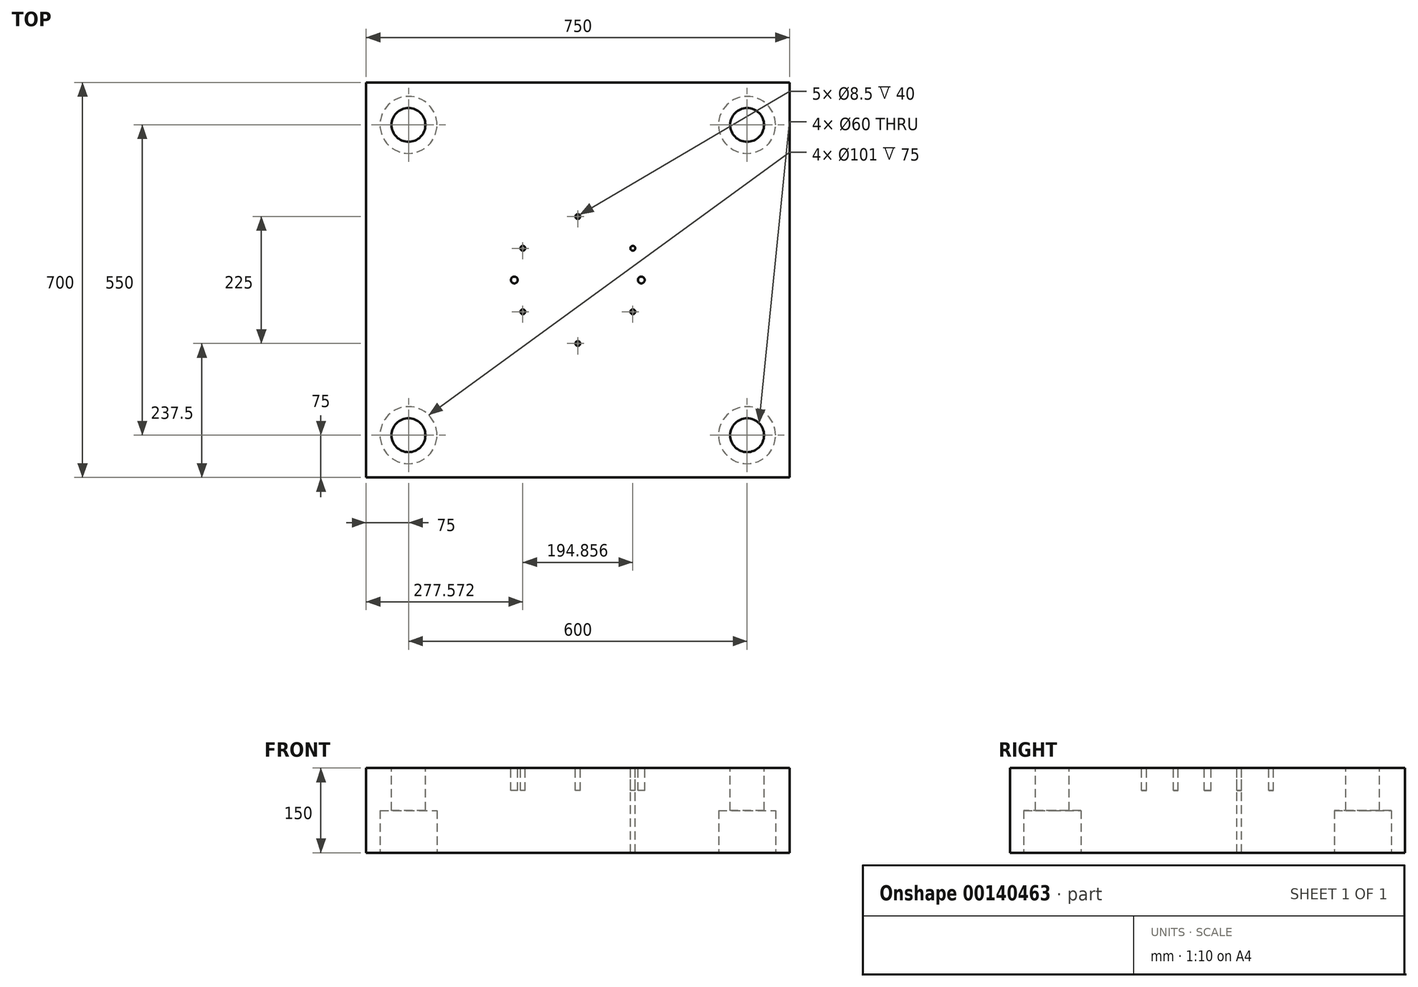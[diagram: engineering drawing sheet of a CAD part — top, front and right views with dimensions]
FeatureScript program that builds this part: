
annotation { "Feature Type Name" : "Feature", "Feature Type Description" : "" }
export const myFeature = defineFeature(function(context is Context, id is Id, definition is map)
    precondition{}
    {
        {
            var Q0;
            Q0=qCreatedBy(makeId("Top.planeOp"),FACE);
            var sketch = newSketch(context, id + "F0", { "sketchPlane" : qUnion([Q0])});
            skLineSegment(sketch, "E0.bottom", {"start": v(375, -350) * mm, "end": v(-375, -350) * mm});
            skLineSegment(sketch, "E0.top", {"start": v(375, 350) * mm, "end": v(-375, 350) * mm});
            skLineSegment(sketch, "E0.left", {"start": v(375, -350) * mm, "end": v(375, 350) * mm});
            skLineSegment(sketch, "E0.right", {"start": v(-375, -350) * mm, "end": v(-375, 350) * mm});
            skPoint(sketch, "E0.middle", {"position": v(0, 0) * mm});
            skCircle(sketch, "E1", {"center": v(-300, -275) * mm, "radius": 30 * mm});
            skCircle(sketch, "E2", {"center": v(300, -275) * mm, "radius": 30 * mm});
            skCircle(sketch, "E3", {"center": v(300, 275) * mm, "radius": 30 * mm});
            skCircle(sketch, "E4", {"center": v(-300, 275) * mm, "radius": 30 * mm});
            skCircle(sketch, "E5", {"center": v(0, 0) * mm, "radius": 112.5 * mm, "construction": true});
            skCircle(sketch, "E6", {"center": v(0, 112.5) * mm, "radius": 4.25 * mm});
            skCircle(sketch, "E7.1.0", {"center": v(-97.43, 56.25) * mm, "radius": 4.25 * mm});
            skCircle(sketch, "E7.2.0", {"center": v(-97.43, -56.25) * mm, "radius": 4.25 * mm});
            skCircle(sketch, "E7.3.0", {"center": v(0, -112.5) * mm, "radius": 4.25 * mm});
            skCircle(sketch, "E7.4.0", {"center": v(97.43, -56.25) * mm, "radius": 4.25 * mm});
            skCircle(sketch, "E7.5.0", {"center": v(97.43, 56.25) * mm, "radius": 4.25 * mm});
            skCircle(sketch, "E8", {"center": v(-112.5, 0) * mm, "radius": 6 * mm});
            skCircle(sketch, "E9", {"center": v(112.5, 0) * mm, "radius": 6 * mm});
            skSolve(sketch);
        }
        {
            var Q0;
            Q0=makeQuery(id+"F0.imprint","IMPRINT",FACE,{"disambiguationData":[TD([[makeQuery(id+"F0.imprint","IMPRINT",EDGE,{"derivedFrom":sQuery(id+"F0.wireOp",EDGE,"E0.bottom")}),-1.0]])]});
            var Q1;
            Q1=makeQuery(id+"F0.imprint","IMPRINT",FACE,{"disambiguationData":[TD([[makeQuery(id+"F0.imprint","IMPRINT",EDGE,{"derivedFrom":sQuery(id+"F0.wireOp",EDGE,"E8")}),1.0]])]});
            var Q2;
            Q2=makeQuery(id+"F0.imprint","IMPRINT",FACE,{"disambiguationData":[TD([[makeQuery(id+"F0.imprint","IMPRINT",EDGE,{"derivedFrom":sQuery(id+"F0.wireOp",EDGE,"E7.2.0")}),1.0]])]});
            var Q3;
            Q3=makeQuery(id+"F0.imprint","IMPRINT",FACE,{"disambiguationData":[TD([[makeQuery(id+"F0.imprint","IMPRINT",EDGE,{"derivedFrom":sQuery(id+"F0.wireOp",EDGE,"E7.1.0")}),1.0]])]});
            var Q4;
            Q4=makeQuery(id+"F0.imprint","IMPRINT",FACE,{"disambiguationData":[TD([[makeQuery(id+"F0.imprint","IMPRINT",EDGE,{"derivedFrom":sQuery(id+"F0.wireOp",EDGE,"E6")}),1.0]])]});
            var Q5;
            Q5=makeQuery(id+"F0.imprint","IMPRINT",FACE,{"disambiguationData":[TD([[makeQuery(id+"F0.imprint","IMPRINT",EDGE,{"derivedFrom":sQuery(id+"F0.wireOp",EDGE,"E9")}),1.0]])]});
            var Q6;
            Q6=makeQuery(id+"F0.imprint","IMPRINT",FACE,{"disambiguationData":[TD([[makeQuery(id+"F0.imprint","IMPRINT",EDGE,{"derivedFrom":sQuery(id+"F0.wireOp",EDGE,"E7.4.0")}),1.0]])]});
            var Q7;
            Q7=makeQuery(id+"F0.imprint","IMPRINT",FACE,{"disambiguationData":[TD([[makeQuery(id+"F0.imprint","IMPRINT",EDGE,{"derivedFrom":sQuery(id+"F0.wireOp",EDGE,"E7.3.0")}),1.0]])]});
            extrude(context, id + "F1", {"entities" : qUnion([Q0, Q1, Q2, Q3, Q4, Q5, Q6, Q7]), "oppositeDirection" : true, "depth" : 150 * mm});
        }
        {
            var Q0;
            Q0=makeQuery(id+"F0.imprint","IMPRINT",FACE,{"disambiguationData":[TD([[makeQuery(id+"F0.imprint","IMPRINT",EDGE,{"derivedFrom":sQuery(id+"F0.wireOp",EDGE,"E4")}),-1.0]])]});
            var Q1;
            Q1=makeQuery(id+"F0.imprint","IMPRINT",FACE,{"disambiguationData":[TD([[makeQuery(id+"F0.imprint","IMPRINT",EDGE,{"derivedFrom":sQuery(id+"F0.wireOp",EDGE,"E3")}),-1.0]])]});
            var Q2;
            Q2=makeQuery(id+"F0.imprint","IMPRINT",FACE,{"disambiguationData":[TD([[makeQuery(id+"F0.imprint","IMPRINT",EDGE,{"derivedFrom":sQuery(id+"F0.wireOp",EDGE,"E2")}),-1.0]])]});
            var Q3;
            Q3=makeQuery(id+"F0.imprint","IMPRINT",FACE,{"disambiguationData":[TD([[makeQuery(id+"F0.imprint","IMPRINT",EDGE,{"derivedFrom":sQuery(id+"F0.wireOp",EDGE,"E1")}),-1.0]])]});
            extrude(context, id + "F2", {"entities" : qUnion([Q0, Q1, Q2, Q3]), "oppositeDirection" : true, "depth" : 130 * mm});
        }
        {
            var Q0;
            Q0=makeQuery(id+"F0.imprint","IMPRINT",FACE,{"disambiguationData":[TD([[makeQuery(id+"F0.imprint","IMPRINT",EDGE,{"derivedFrom":sQuery(id+"F0.wireOp",EDGE,"E8")}),1.0]])]});
            var Q1;
            Q1=makeQuery(id+"F0.imprint","IMPRINT",FACE,{"disambiguationData":[TD([[makeQuery(id+"F0.imprint","IMPRINT",EDGE,{"derivedFrom":sQuery(id+"F0.wireOp",EDGE,"E7.1.0")}),1.0]])]});
            var Q2;
            Q2=makeQuery(id+"F0.imprint","IMPRINT",FACE,{"disambiguationData":[TD([[makeQuery(id+"F0.imprint","IMPRINT",EDGE,{"derivedFrom":sQuery(id+"F0.wireOp",EDGE,"E6")}),1.0]])]});
            var Q3;
            Q3=makeQuery(id+"F0.imprint","IMPRINT",FACE,{"disambiguationData":[TD([[makeQuery(id+"F0.imprint","IMPRINT",EDGE,{"derivedFrom":sQuery(id+"F0.wireOp",EDGE,"E7.5.0")}),1.0]])]});
            var Q4;
            Q4=makeQuery(id+"F0.imprint","IMPRINT",FACE,{"disambiguationData":[TD([[makeQuery(id+"F0.imprint","IMPRINT",EDGE,{"derivedFrom":sQuery(id+"F0.wireOp",EDGE,"E9")}),1.0]])]});
            var Q5;
            Q5=makeQuery(id+"F0.imprint","IMPRINT",FACE,{"disambiguationData":[TD([[makeQuery(id+"F0.imprint","IMPRINT",EDGE,{"derivedFrom":sQuery(id+"F0.wireOp",EDGE,"E7.4.0")}),1.0]])]});
            var Q6;
            Q6=makeQuery(id+"F0.imprint","IMPRINT",FACE,{"disambiguationData":[TD([[makeQuery(id+"F0.imprint","IMPRINT",EDGE,{"derivedFrom":sQuery(id+"F0.wireOp",EDGE,"E7.3.0")}),1.0]])]});
            var Q7;
            Q7=makeQuery(id+"F0.imprint","IMPRINT",FACE,{"disambiguationData":[TD([[makeQuery(id+"F0.imprint","IMPRINT",EDGE,{"derivedFrom":sQuery(id+"F0.wireOp",EDGE,"E7.2.0")}),1.0]])]});
            extrude(context, id + "F3", {"entities" : qUnion([Q0, Q1, Q2, Q3, Q4, Q5, Q6, Q7]), "operationType" : NewBodyOperationType.REMOVE, "oppositeDirection" : true, "depth" : 40 * mm});
        }
        {
            var Q0;
            Q0=makeQuery(id+"F2.opExtrude","SWEPT_BODY",BODY,{"disambiguationData":[OSD([sQuery(id+"F0.wireOp",EDGE,"E3"),sQuery(id+"F0.wireOp",EDGE,"0WcaU4d4-yjLl-t4DH-PHqA-r2zW4oB6RqLG")])]});
            var Q1;
            Q1=makeQuery(id+"F2.opExtrude","SWEPT_BODY",BODY,{"disambiguationData":[OSD([sQuery(id+"F0.wireOp",EDGE,"E2"),sQuery(id+"F0.wireOp",EDGE,"WCeEpNrA-Mq1f-Tu2g-0Etf-8BQyyMGswOfX")])]});
            var Q2;
            Q2=makeQuery(id+"F2.opExtrude","SWEPT_BODY",BODY,{"disambiguationData":[OSD([sQuery(id+"F0.wireOp",EDGE,"E1"),sQuery(id+"F0.wireOp",EDGE,"xFfE00Wn-gLOv-J7tR-mGqZ-GsZgmZ165pkX")])]});
            var Q3;
            Q3=makeQuery(id+"F2.opExtrude","SWEPT_BODY",BODY,{"disambiguationData":[OSD([sQuery(id+"F0.wireOp",EDGE,"E4"),sQuery(id+"F0.wireOp",EDGE,"XaCNIt4j-slsJ-z5ex-szqA-43I0Ko6RFmIr")])]});
            transform(context, id + "F4", {"entities" : qUnion([Q0, Q1, Q2, Q3]), "transformType" : TransformType.TRANSLATION_3D, "dx" : 0 * mm, "dy" : 0 * mm, "dz" : -20 * mm, "makeCopy" : false});
        }
        {
            var Q0;
            Q0=makeQuery(id+"F2.opExtrude","SWEPT_BODY",BODY,{"disambiguationData":[OSD([sQuery(id+"F0.wireOp",EDGE,"E3"),sQuery(id+"F0.wireOp",EDGE,"0WcaU4d4-yjLl-t4DH-PHqA-r2zW4oB6RqLG")])]});
            var Q1;
            Q1=makeQuery(id+"F2.opExtrude","SWEPT_BODY",BODY,{"disambiguationData":[OSD([sQuery(id+"F0.wireOp",EDGE,"E2"),sQuery(id+"F0.wireOp",EDGE,"WCeEpNrA-Mq1f-Tu2g-0Etf-8BQyyMGswOfX")])]});
            var Q2;
            Q2=makeQuery(id+"F2.opExtrude","SWEPT_BODY",BODY,{"disambiguationData":[OSD([sQuery(id+"F0.wireOp",EDGE,"E4"),sQuery(id+"F0.wireOp",EDGE,"XaCNIt4j-slsJ-z5ex-szqA-43I0Ko6RFmIr")])]});
            var Q3;
            Q3=makeQuery(id+"F2.opExtrude","SWEPT_BODY",BODY,{"disambiguationData":[OSD([sQuery(id+"F0.wireOp",EDGE,"E1"),sQuery(id+"F0.wireOp",EDGE,"xFfE00Wn-gLOv-J7tR-mGqZ-GsZgmZ165pkX")])]});
            var Q4;
            Q4=makeQuery(id+"F1.opExtrude","SWEPT_BODY",BODY,{"disambiguationData":[OSD([sQuery(id+"F0.wireOp",EDGE,"E0.bottom"),sQuery(id+"F0.wireOp",EDGE,"E0.top"),sQuery(id+"F0.wireOp",EDGE,"E0.left"),sQuery(id+"F0.wireOp",EDGE,"E0.right"),sQuery(id+"F0.wireOp",EDGE,"xFfE00Wn-gLOv-J7tR-mGqZ-GsZgmZ165pkX"),sQuery(id+"F0.wireOp",EDGE,"XaCNIt4j-slsJ-z5ex-szqA-43I0Ko6RFmIr"),sQuery(id+"F0.wireOp",EDGE,"WCeEpNrA-Mq1f-Tu2g-0Etf-8BQyyMGswOfX"),sQuery(id+"F0.wireOp",EDGE,"0WcaU4d4-yjLl-t4DH-PHqA-r2zW4oB6RqLG"),sQuery(id+"F0.wireOp",EDGE,"E7.5.0")])]});
            booleanBodies(context, id + "F5", {"operationType" : BooleanOperationType.UNION, "tools" : qUnion([Q0, Q1, Q2, Q3, Q4])});
        }
        {
            var Q0;
            {var subQ0=sQuery(id+"F0.wireOp",EDGE,"E7.5.0");var subQ1=sQuery(id+"F0.wireOp",EDGE,"E4");var subQ2=sQuery(id+"F0.wireOp",EDGE,"E3");var subQ3=sQuery(id+"F0.wireOp",EDGE,"E2");var subQ4=sQuery(id+"F0.wireOp",EDGE,"E1");var subQ5=sQuery(id+"F0.wireOp",EDGE,"E0.right");var subQ6=sQuery(id+"F0.wireOp",EDGE,"E0.left");var subQ7=sQuery(id+"F0.wireOp",EDGE,"E0.top");var subQ8=sQuery(id+"F0.wireOp",EDGE,"E0.bottom");Q0=makeQuery(id+"F5.opBoolean","MERGE",FACE,{"derivedFrom":[makeQuery(id+"F1.opExtrude","CAP_FACE",FACE,{"disambiguationData":[OSD([subQ8,subQ7,subQ6,subQ5,subQ4,subQ3,subQ2,subQ1,subQ0])],"isStart":false}),makeQuery(id+"F2.opExtrude","CAP_FACE",FACE,{"disambiguationData":[OSD([subQ8,subQ7,subQ6,subQ5,subQ4,subQ3,subQ2,subQ1,sQuery(id+"F0.wireOp",EDGE,"E6"),sQuery(id+"F0.wireOp",EDGE,"E7.1.0"),sQuery(id+"F0.wireOp",EDGE,"E7.2.0"),sQuery(id+"F0.wireOp",EDGE,"E7.3.0"),sQuery(id+"F0.wireOp",EDGE,"E7.4.0"),subQ0,sQuery(id+"F0.wireOp",EDGE,"E8"),sQuery(id+"F0.wireOp",EDGE,"E9")])],"isStart":false})]});}
            var sketch = newSketch(context, id + "F6", { "sketchPlane" : qUnion([Q0])});
            skPoint(sketch, "E10", {"position": v(-300, 275) * mm});
            skPoint(sketch, "E11", {"position": v(300, 275) * mm});
            skPoint(sketch, "E12", {"position": v(300, -275) * mm});
            skPoint(sketch, "E13", {"position": v(-300, -275) * mm});
            skCircle(sketch, "E14", {"center": v(-300, 275) * mm, "radius": 50.5 * mm});
            skCircle(sketch, "E15", {"center": v(-300, -275) * mm, "radius": 50.5 * mm});
            skCircle(sketch, "E16", {"center": v(300, -275) * mm, "radius": 50.5 * mm});
            skCircle(sketch, "E17", {"center": v(300, 275) * mm, "radius": 50.5 * mm});
            skSolve(sketch);
        }
        {
            var Q0;
            Q0=makeQuery(id+"F6.imprint","IMPRINT",FACE,{"disambiguationData":[TD([[makeQuery(id+"F6.imprint","IMPRINT",EDGE,{"derivedFrom":sQuery(id+"F6.wireOp",EDGE,"E14")}),1.0]])]});
            var Q1;
            Q1=makeQuery(id+"F6.imprint","IMPRINT",FACE,{"disambiguationData":[TD([[makeQuery(id+"F6.imprint","IMPRINT",EDGE,{"derivedFrom":sQuery(id+"F6.wireOp",EDGE,"E15")}),1.0]])]});
            var Q2;
            Q2=makeQuery(id+"F6.imprint","IMPRINT",FACE,{"disambiguationData":[TD([[makeQuery(id+"F6.imprint","IMPRINT",EDGE,{"derivedFrom":sQuery(id+"F6.wireOp",EDGE,"E16")}),1.0]])]});
            var Q3;
            Q3=makeQuery(id+"F6.imprint","IMPRINT",FACE,{"disambiguationData":[TD([[makeQuery(id+"F6.imprint","IMPRINT",EDGE,{"derivedFrom":sQuery(id+"F6.wireOp",EDGE,"E17")}),1.0]])]});
            extrude(context, id + "F7", {"entities" : qUnion([Q0, Q1, Q2, Q3]), "operationType" : NewBodyOperationType.REMOVE, "oppositeDirection" : true, "depth" : 75 * mm});
        }
    });
